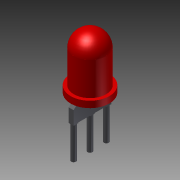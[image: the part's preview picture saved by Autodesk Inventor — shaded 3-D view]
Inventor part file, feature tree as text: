
AUTODESK INVENTOR PART (.ipt)
format: ipt  version: 2012 (Build 160160000, 160)  size: 165,376 bytes
history: native  units: mm
features: sketch x7, extrude x6, revolve x1
ambient origin geometry x8: Origin, YZ Plane, XZ Plane, XY Plane, X Axis, Y Axis, Z Axis, Center Point
bodies: Solid1 (feature_tree)
feature tree (14):
  extrude  "Extrusion1"  Depth=5.1mm TaperAngle=0.0deg
  extrude  "Extrusion2"  Depth=1.0mm TaperAngle=0.0deg
  revolve  "Revolution1"  [1 undecoded]
  extrude  "Extrusion3"  Depth=0.75mm
  sketch  "Sketch6"  dims[d15=0.75mm d16=0.75mm]
  sketch  "Sketch7"  dims[d17=2.54mm d18=2.54mm]
  extrude  "Extrusion4"  Depth=0.75mm
  extrude  "Extrusion5"  Depth=2.54mm
  extrude  "Extrusion6"  Depth=4.5mm
  sketch  "Sketch1"  dims[d0=5.0mm d1=5.1mm d2=0.0mm]
  sketch  "Sketch2"  dims[d3=6.0mm d4=1.0mm d5=0.0mm]
  sketch  "Sketch4"  dims[d11=2.5mm d12=5.0mm]
  sketch  "Sketch5"  dims[d13=90.0deg d14=0.75mm]
  sketch  "Sketch8"  dims[d19=2.75mm d20=4.5mm d21=0.75mm d22=0.75mm d23=0.1mm d24=0.0mm d25=0.375mm d26=0.75mm d27=0.0mm d28=5.0mm d29=0.0mm d30=5.0mm d31=0.0mm d32=5.0mm d33=0.0mm]
note: 1 required parameter value undecoded (feature->parameter linkage not recoverable at this tier; creation-order binding heuristic only, values carry confidence <= 0.55)
